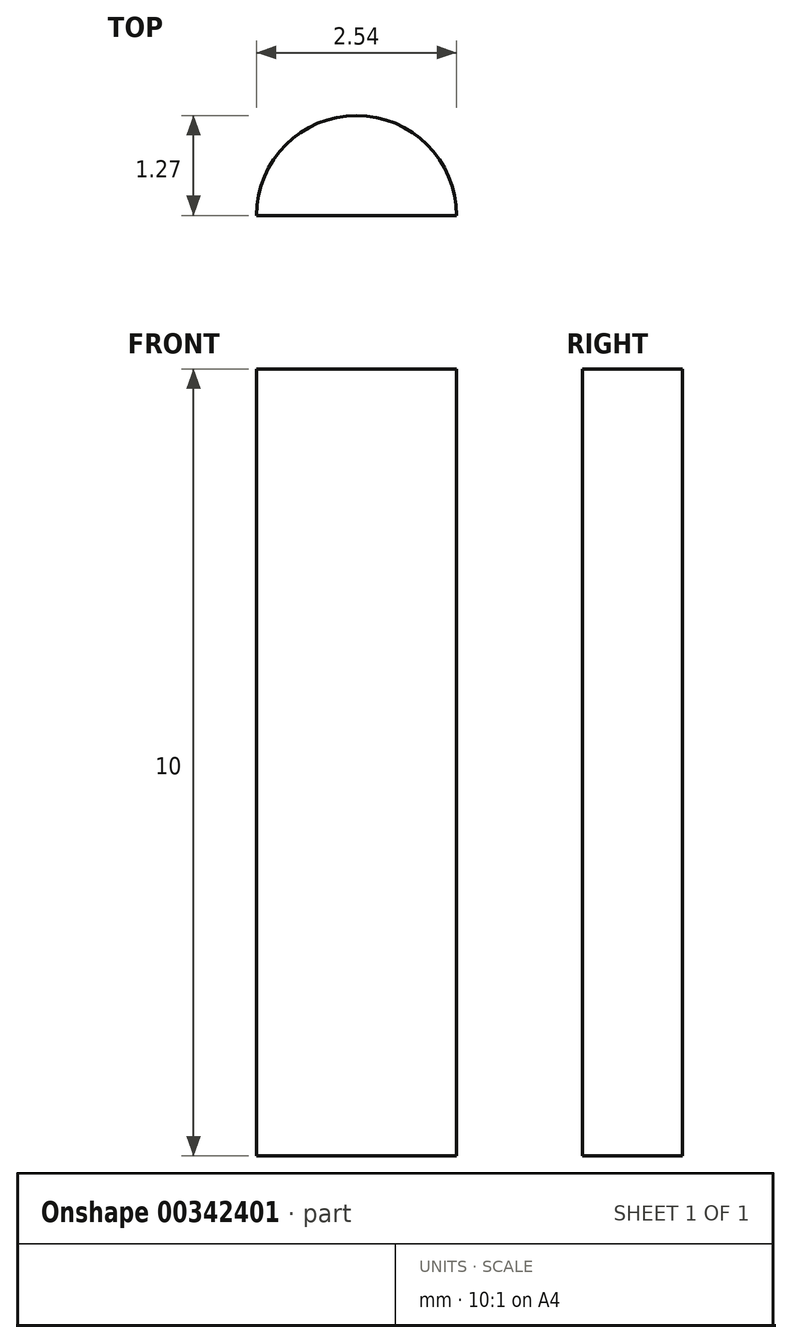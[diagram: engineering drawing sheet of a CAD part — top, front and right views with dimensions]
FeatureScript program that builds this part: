
annotation { "Feature Type Name" : "Feature", "Feature Type Description" : "" }
export const myFeature = defineFeature(function(context is Context, id is Id, definition is map)
    precondition{}
    {
        {
            var Q0;
            Q0=qCreatedBy(makeId("Top.planeOp"),FACE);
            var sketch = newSketch(context, id + "F0", { "sketchPlane" : qUnion([Q0])});
            skCircle(sketch, "E0", {"center": v(0, 0) * mm, "radius": 1.27 * mm});
            skSolve(sketch);
        }
        {
            var Q0;
            Q0=qSketchRegion(id+"F0",true);
            extrude(context, id + "F1", {"entities" : qUnion([Q0]), "depth" : 10 * mm});
        }
        {
            var Q0;
            Q0=qCreatedBy(makeId("Top.planeOp"),FACE);
            cPlane(context, id + "F2", {"entities" : qUnion([Q0]), "cplaneType" : CPlaneType.OFFSET, "offset" : 44.96 * mm, "width" : 152.4 * mm, "height" : 152.4 * mm});
        }
        {
            var Q0;
            Q0=qCreatedBy(id+"F2.planeOp",FACE);
            var sketch = newSketch(context, id + "F3", { "sketchPlane" : qUnion([Q0])});
            skArc(sketch, "E1", {"start": v(-1.55, 0) * mm, "mid": v(0.04, -2.12) * mm, "end": v(1.63, 0) * mm});
            skLineSegment(sketch, "E2", {"start": v(-1.55, 0) * mm, "end": v(1.63, 0) * mm});
            skSolve(sketch);
        }
        {
            var Q0;
            Q0 = qSketchRegion(id + "F3", true);
            extrude(context, id + "F4", {"entities" : qUnion([Q0]), "operationType" : NewBodyOperationType.REMOVE, "oppositeDirection" : true, "depth" : 98.04 * mm});
        }
    });
